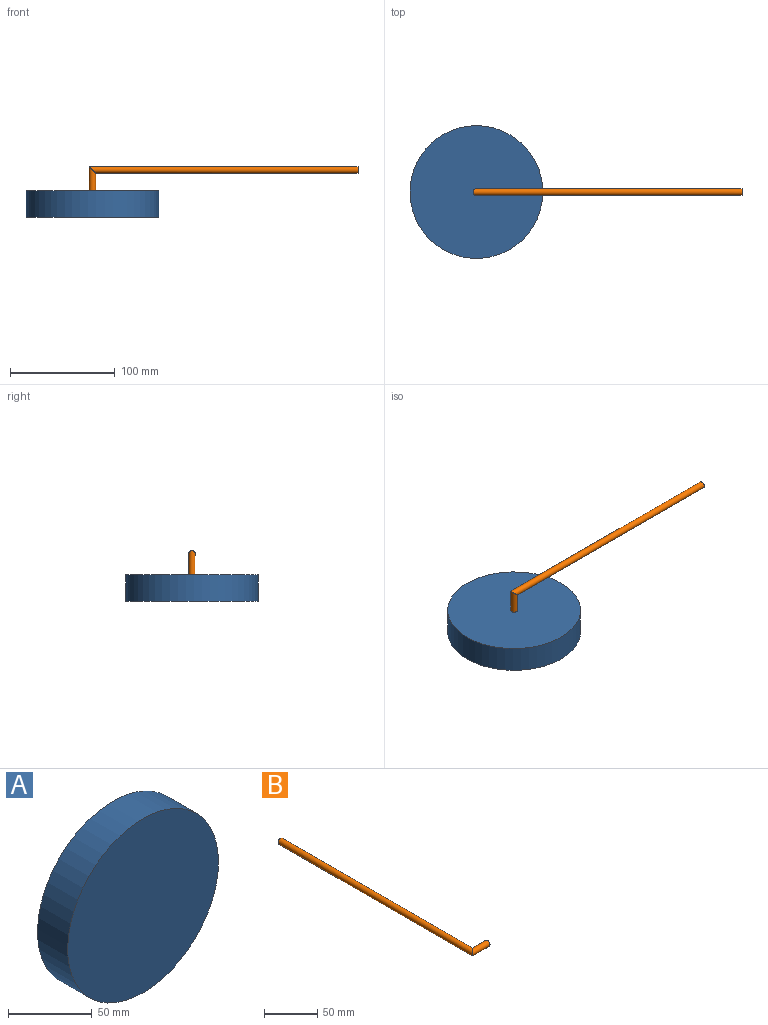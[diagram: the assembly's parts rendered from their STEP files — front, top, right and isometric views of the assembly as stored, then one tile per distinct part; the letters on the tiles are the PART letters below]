
ASSEMBLY  parts=2 mates=1
PART A: 3 faces, bbox 127x25.4x127 mm
  f0: cylinder r=63.5mm len=127mm, axis (0,1,0), area 10134.1mm2, adj f1,f2
  f1: plane 127x127mm, normal (0,-1,0), area 12667.7mm2, adj f0
  f2: plane 127x127mm, normal (0,1,0), area 12667.7mm2, adj f0
PART B: 4 faces, bbox 23.2x257.2x6.4 mm
  f0: plane 6.35x6.35mm, normal (1,0,0), area 31.7mm2, adj f2
  f1: plane 6.35x6.35mm, normal (0,1,0), area 31.7mm2, adj f3
  f2: cylinder r=3.17mm len=23.18mm, axis (1,0,0), area 396.8mm2, adj f0,f3
  f3: cylinder r=3.17mm len=257.18mm, axis (0,-1,0), area 5064.9mm2, adj f1,f2
PLACE A rot(axis=(1,0,0),90deg) t=(0,0,-12.7)mm
PLACE B rot(axis=(0.58,0.58,-0.58),120deg) t=(254,0,20)mm
MATE fastened B.f2 <-> A.f0  axis (0,0,-1) through (0,0,0)mm
